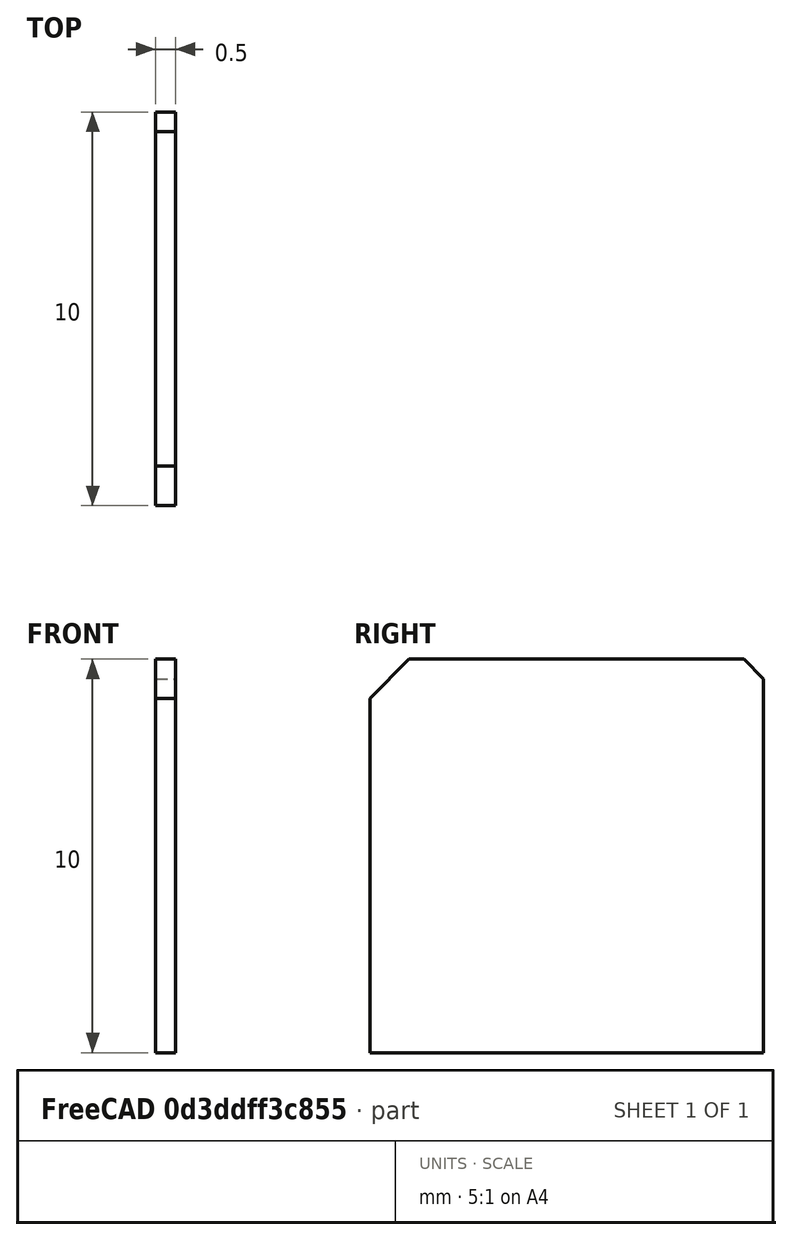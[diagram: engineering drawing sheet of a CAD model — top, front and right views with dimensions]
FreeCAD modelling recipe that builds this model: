
FCSTD DOCUMENT  (FreeCAD 1.1R20260108 (Git shallow))
Label: LiNbO3_Substrate_10mm
License: All rights reserved
LicenseURL: https://en.wikipedia.org/wiki/All_rights_reserved
objects: TechDraw::DrawViewDimension×6, TechDraw::DrawViewAnnotation×3, TechDraw::DrawProjGroupItem×2, App::Point×1, Sketcher::SketchObject×1, PartDesign::Pad×1, PartDesign::Body×1, TechDraw::DrawSVGTemplate×1, TechDraw::DrawProjGroup×1, TechDraw::DrawPage×1
note: 18 computed .brp shape members not serialized (recipe doc carries the construction recipe); baked Part::Feature solids carry a one-line shape summary decoded from their .brp

FEATURE [App::Point] Origin001
  Role = Origin
FEATURE [Sketcher::SketchObject] Sketch
  ArcFitTolerance = 1e-06
  AttachmentSupport = -> [Origin]
  ExternalTypes = [0]
  FullyConstrained = true
  MakeInternals = false
  MapMode = 5
  Placement = pos=(0,0,0) rot=(0.57735,0.57735,0.57735;2.0944rad)
  sketch-geometry (10):
    g0: LineSegment [constr] StartX=-5 StartY=-5 StartZ=0 EndX=5 EndY=-5 EndZ=0
    g1: LineSegment [constr] StartX=5 StartY=-5 StartZ=0 EndX=5 EndY=5 EndZ=0
    g2: LineSegment [constr] StartX=5 StartY=5 StartZ=0 EndX=-5 EndY=5 EndZ=0
    g3: LineSegment [constr] StartX=-5 StartY=5 StartZ=0 EndX=-5 EndY=-5 EndZ=0
    g4: LineSegment StartX=-5 StartY=-5 StartZ=0 EndX=5 EndY=-5 EndZ=0
    g5: LineSegment StartX=5 StartY=-5 StartZ=0 EndX=5 EndY=4.5 EndZ=0
    g6: LineSegment StartX=-5 StartY=-5 StartZ=0 EndX=-5 EndY=4 EndZ=0
    g7: LineSegment StartX=-4 StartY=5 StartZ=0 EndX=4.5 EndY=5 EndZ=0
    g8: LineSegment StartX=-4 StartY=5 StartZ=0 EndX=-5 EndY=4 EndZ=0
    g9: LineSegment StartX=4.5 StartY=5 StartZ=0 EndX=5 EndY=4.5 EndZ=0
  constraints (28):
    c: Coincident(g0,g1)
    c: Coincident(g1,g2)
    c: Coincident(g2,g3)
    c: Coincident(g3,g0)
    c: Horizontal(g0)
    c: Horizontal(g2)
    c: Vertical(g1)
    c: Vertical(g3)
    c: Equal(g3,g2)
    c: Distance(g2,g2) = 10
    c: DistanceX(g-2,g2) = -5
    c: DistanceY(g-1,g0) = -5
    c: Coincident(g4,g0)
    c: Coincident(g4,g0)
    c: Coincident(g5,g0)
    c: PointOnObject(g5,g1)
    c: Coincident(g6,g0)
    c: PointOnObject(g6,g3)
    c: PointOnObject(g7,g2)
    c: PointOnObject(g7,g2)
    c: Coincident(g8,g7)
    c: Coincident(g8,g6)
    c: Coincident(g9,g7)
    c: Coincident(g9,g5)
    c: Distance(g6,g2) = 1
    c: Distance(g2,g7) = 1
    c: Distance(g5,g1) = 0.5
    c: Distance(g1,g7) = 0.5
FEATURE [PartDesign::Pad] Pad
  Direction = (1,0,0)
  Length = 0.5
  Length2 = 10
  Profile = -> Sketch
  ReferenceAxis = -> Sketch [N_Axis]
  Refine = true
  SideType = 0
  Suppressed = false
  Type = 0
  Type2 = 0
FEATURE [PartDesign::Body] Body
  AllowCompound = false
  Group = -> [Sketch,Pad]
  Origin = -> Origin
  Tip = -> Pad
FEATURE [TechDraw::DrawSVGTemplate] Template
  Height = 210
  Orientation = 1
  Template = /Applications/FreeCAD.app/Contents/Resources/share/Mod/TechDraw/Templates/ISO/A4_Landscape_TD.svg
  Width = 297
FEATURE [TechDraw::DrawProjGroupItem] ProjItem  label="Front"
  CoarseView = false
  Direction = (1,0,0)
  Focus = 100
  HardHidden = true
  IsoCount = 0
  IsoHidden = false
  IsoVisible = false
  LockPosition = true
  Perspective = false
  Rotation = 0
  RotationVector = (0,1,0)
  Scale = 5
  ScaleType = 2
  ScrubCount = 1
  SeamHidden = false
  SeamVisible = false
  SmoothHidden = false
  SmoothVisible = true
  Source = -> [Body]
  Type = 0
  X = 0
  XDirection = (0,1,0)
  Y = 0
FEATURE [TechDraw::DrawProjGroupItem] ProjItem001  label="FrontTopRight"
  CoarseView = false
  Direction = (0.57735,0.57735,0.57735)
  Focus = 100
  HardHidden = true
  IsoCount = 0
  IsoHidden = false
  IsoVisible = false
  LockPosition = false
  Perspective = false
  Rotation = 0
  RotationVector = (1,0,0)
  Scale = 5
  ScaleType = 2
  ScrubCount = 1
  SeamHidden = false
  SeamVisible = false
  SmoothHidden = false
  SmoothVisible = true
  Source = -> [Body]
  Type = 7
  X = -58.5616
  XDirection = (-0.707107,0.707107,0)
  Y = -70.1083
FEATURE [TechDraw::DrawProjGroup] ProjGroup
  Anchor = -> ProjItem
  AutoDistribute = true
  LockPosition = false
  ProjectionType = 0
  Rotation = 0
  Scale = 5
  ScaleType = 2
  Source = -> [Body]
  Views = -> [ProjItem,ProjItem001]
  X = 148.077
  Y = 134.929
  spacingX = 15
  spacingY = 15
FEATURE [TechDraw::DrawViewDimension] Dimension
  AngleOverride = false
  Arbitrary = false
  ArbitraryTolerances = false
  BoxCorners = (2) [(-25,-25,0),(25,25,0)]
  EqualTolerance = true
  ExtensionAngle = 0
  FormatSpec = %.2w
  FormatSpecOverTolerance = %+.2w
  FormatSpecUnderTolerance = %+.2w
  Inverted = false
  LineAngle = 0
  LockPosition = false
  MeasureType = 1
  OverTolerance = 0
  References2D = -> [ProjItem]
  Rotation = 0
  ScaleType = 0
  ShowUnits = false
  TheoreticalExact = false
  Type = 1
  UnderTolerance = 0
  UseActualArea = true
  X = -5.41575
  Y = -12.2703
FEATURE [TechDraw::DrawViewDimension] Dimension001
  AngleOverride = false
  Arbitrary = false
  ArbitraryTolerances = false
  BoxCorners = (2) [(-25,-25,0),(25,25,0)]
  EqualTolerance = true
  ExtensionAngle = 0
  FormatSpec = %.2w
  FormatSpecOverTolerance = %+.2w
  FormatSpecUnderTolerance = %+.2w
  Inverted = false
  LineAngle = 0
  LockPosition = false
  MeasureType = 1
  OverTolerance = 0
  References2D = -> [ProjItem]
  Rotation = 0
  ScaleType = 0
  ShowUnits = false
  TheoreticalExact = false
  Type = 2
  UnderTolerance = 0
  UseActualArea = true
  X = 9.26151
  Y = 4.51312
FEATURE [TechDraw::DrawViewDimension] Dimension002
  AngleOverride = false
  Arbitrary = false
  ArbitraryTolerances = false
  BoxCorners = (2) [(-25,-25,0),(25,25,0)]
  EqualTolerance = true
  ExtensionAngle = 0
  FormatSpec = %.2w
  FormatSpecOverTolerance = %+.2w
  FormatSpecUnderTolerance = %+.2w
  Inverted = false
  LineAngle = 0
  LockPosition = false
  MeasureType = 1
  OverTolerance = 0.1
  References2D = -> [ProjItem]
  Rotation = 0
  ScaleType = 0
  ShowUnits = false
  TheoreticalExact = false
  Type = 2
  UnderTolerance = -0.1
  UseActualArea = true
  X = 35.4748
  Y = 5.37843
FEATURE [TechDraw::DrawViewDimension] Dimension003
  AngleOverride = false
  Arbitrary = false
  ArbitraryTolerances = false
  BoxCorners = (2) [(-25,-25,0),(25,25,0)]
  EqualTolerance = true
  ExtensionAngle = 0
  FormatSpec = %.2w
  FormatSpecOverTolerance = %+.2w
  FormatSpecUnderTolerance = %+.2w
  Inverted = false
  LineAngle = 0
  LockPosition = false
  MeasureType = 1
  OverTolerance = 0.1
  References2D = -> [ProjItem]
  Rotation = 0
  ScaleType = 0
  ShowUnits = false
  TheoreticalExact = false
  Type = 1
  UnderTolerance = -0.1
  UseActualArea = true
  X = 37.996
  Y = 41.3764
FEATURE [TechDraw::DrawViewDimension] Dimension004
  AngleOverride = false
  Arbitrary = false
  ArbitraryTolerances = false
  BoxCorners = (2) [(-25,-25,0),(25,25,0)]
  EqualTolerance = true
  ExtensionAngle = 0
  FormatSpec = %.2w
  FormatSpecOverTolerance = %+.2w
  FormatSpecUnderTolerance = %+.2w
  Inverted = false
  LineAngle = 0
  LockPosition = false
  MeasureType = 1
  OverTolerance = 0.1
  References2D = -> [ProjItem]
  Rotation = 0
  ScaleType = 0
  ShowUnits = false
  TheoreticalExact = false
  Type = 2
  UnderTolerance = -0.1
  UseActualArea = true
  X = -38.51
  Y = -5.67511
FEATURE [TechDraw::DrawViewDimension] Dimension005
  AngleOverride = false
  Arbitrary = false
  ArbitraryTolerances = false
  BoxCorners = (2) [(-25,-25,0),(25,25,0)]
  EqualTolerance = true
  ExtensionAngle = 0
  FormatSpec = %.2w
  FormatSpecOverTolerance = %+.2w
  FormatSpecUnderTolerance = %+.2w
  Inverted = false
  LineAngle = 0
  LockPosition = false
  MeasureType = 1
  OverTolerance = 0.1
  References2D = -> [ProjItem]
  Rotation = 0
  ScaleType = 0
  ShowUnits = false
  TheoreticalExact = false
  Type = 1
  UnderTolerance = -0.1
  UseActualArea = true
  X = -40.6993
  Y = 41.3764
FEATURE [TechDraw::DrawViewAnnotation] Annotation
  Font = osifont
  LineSpace = 100
  LockPosition = false
  MaxWidth = -1
  Rotation = 0
  ScaleType = 0
  Text = +X
  TextSize = 5
  TextStyle = 0
  X = 56.9585
  Y = 47.7582
FEATURE [TechDraw::DrawViewAnnotation] Annotation001
  Font = osifont
  LineSpace = 100
  LockPosition = false
  MaxWidth = -1
  Rotation = 0
  ScaleType = 0
  Text = +Y
  TextSize = 5
  TextStyle = 0
  X = 122.657
  Y = 45.6812
FEATURE [TechDraw::DrawViewAnnotation] Annotation002
  Font = osifont
  LineSpace = 100
  LockPosition = false
  MaxWidth = -1
  Rotation = 0
  ScaleType = 0
  Text = +Z
  TextSize = 5
  TextStyle = 0
  X = 89.5157
  Y = 103.707
FEATURE [TechDraw::DrawPage] Page
  KeepUpdated = true
  NextBalloonIndex = 1
  ProjectionType = 0
  Template = -> Template
  Views = -> [ProjGroup,Dimension,Dimension001,Dimension002,Dimension003,Dimension004,Dimension005,Annotation,Annotation001,Annotation002]
